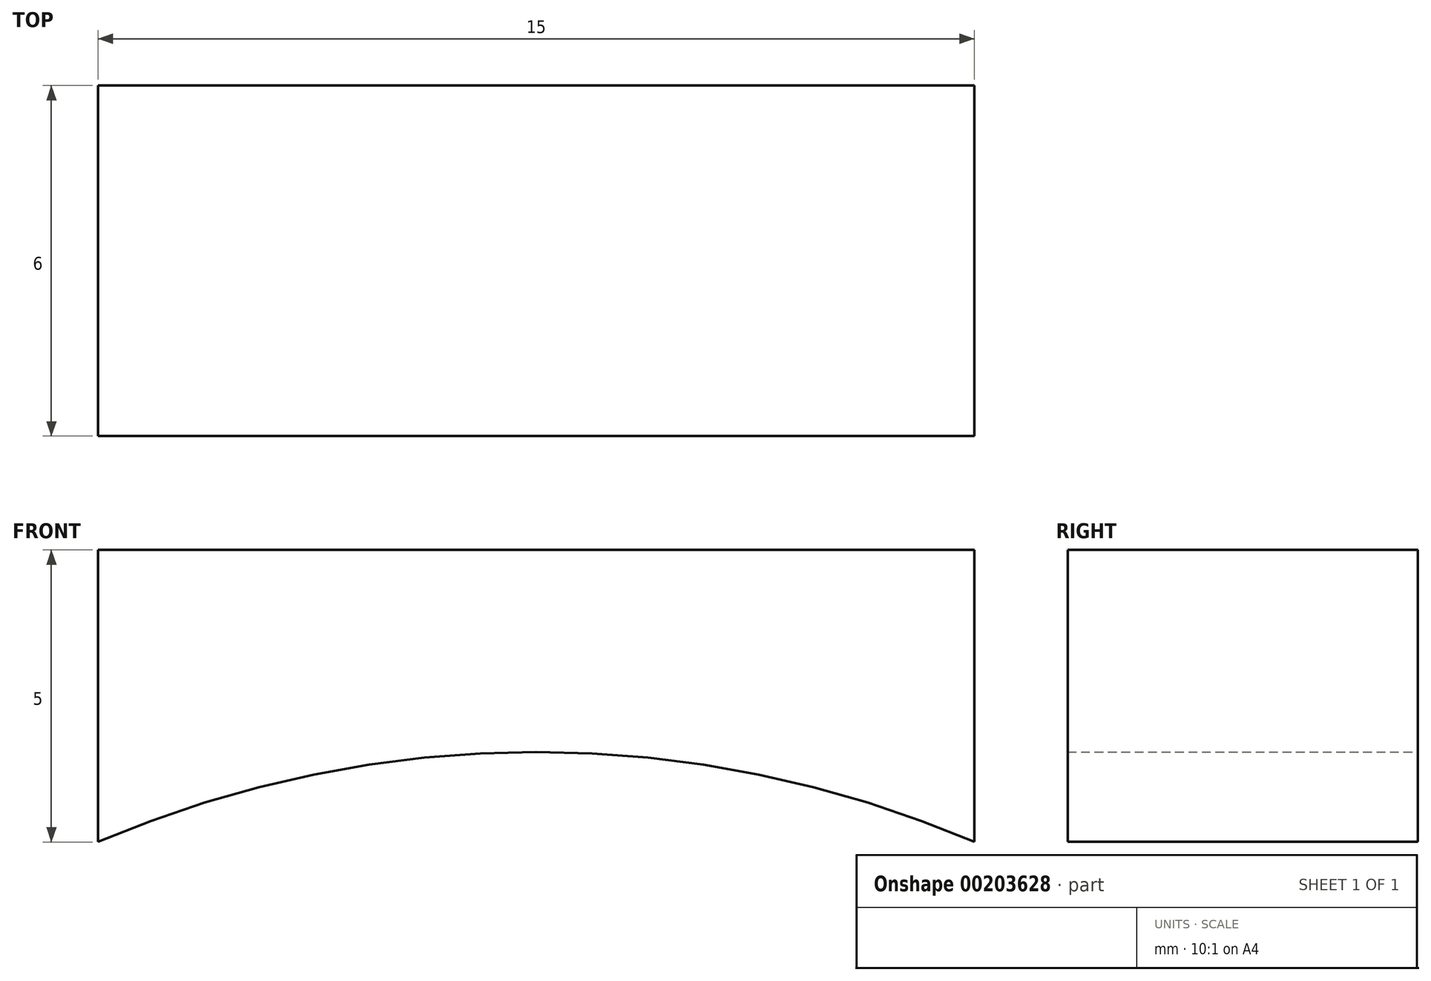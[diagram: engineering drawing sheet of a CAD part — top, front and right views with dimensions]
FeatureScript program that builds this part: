
annotation { "Feature Type Name" : "Feature", "Feature Type Description" : "" }
export const myFeature = defineFeature(function(context is Context, id is Id, definition is map)
    precondition{}
    {
        {
            var Q0;
            Q0=qCreatedBy(makeId("Front.planeOp"),FACE);
            var sketch = newSketch(context, id + "F0", { "sketchPlane" : qUnion([Q0])});
            skCircle(sketch, "E0", {"center": v(0, 0) * mm, "radius": 19.05 * mm});
            skLineSegment(sketch, "E1.bottom", {"start": v(-7.5, 22.51) * mm, "end": v(7.5, 22.51) * mm});
            skLineSegment(sketch, "E1.left", {"start": v(-7.5, 22.51) * mm, "end": v(-7.5, 17.51) * mm});
            skLineSegment(sketch, "E1.right", {"start": v(7.5, 22.51) * mm, "end": v(7.5, 17.51) * mm});
            skLineSegment(sketch, "E2.bottom", {"start": v(-0.5, 22.51) * mm, "end": v(0.5, 22.51) * mm});
            skLineSegment(sketch, "E2.top", {"start": v(-0.5, 30.51) * mm, "end": v(0.5, 30.51) * mm});
            skLineSegment(sketch, "E2.left", {"start": v(-0.5, 22.51) * mm, "end": v(-0.5, 30.51) * mm});
            skLineSegment(sketch, "E2.right", {"start": v(0.5, 22.51) * mm, "end": v(0.5, 30.51) * mm});
            skSolve(sketch);
        }
        {
            var Q0;
            {var subQ0=sQuery(id+"F0.wireOp",EDGE,"E1.left");Q0=makeQuery(id+"F0.imprint","IMPRINT",FACE,{"disambiguationData":[TD([[makeQuery(id+"F0.imprint","IMPRINT",EDGE,{"derivedFrom":subQ0}),1.0]])]});}
            var Q1;
            Q1=makeQuery(id+"F0.imprint","IMPRINT",FACE,{"disambiguationData":[TD([[makeQuery(id+"F0.imprint","IMPRINT",EDGE,{"derivedFrom":sQuery(id+"F0.wireOp",EDGE,"E2.bottom")}),1.0]])]});
            extrude(context, id + "F1", {"entities" : qUnion([Q0, Q1]), "depth" : 6 * mm});
        }
    });
